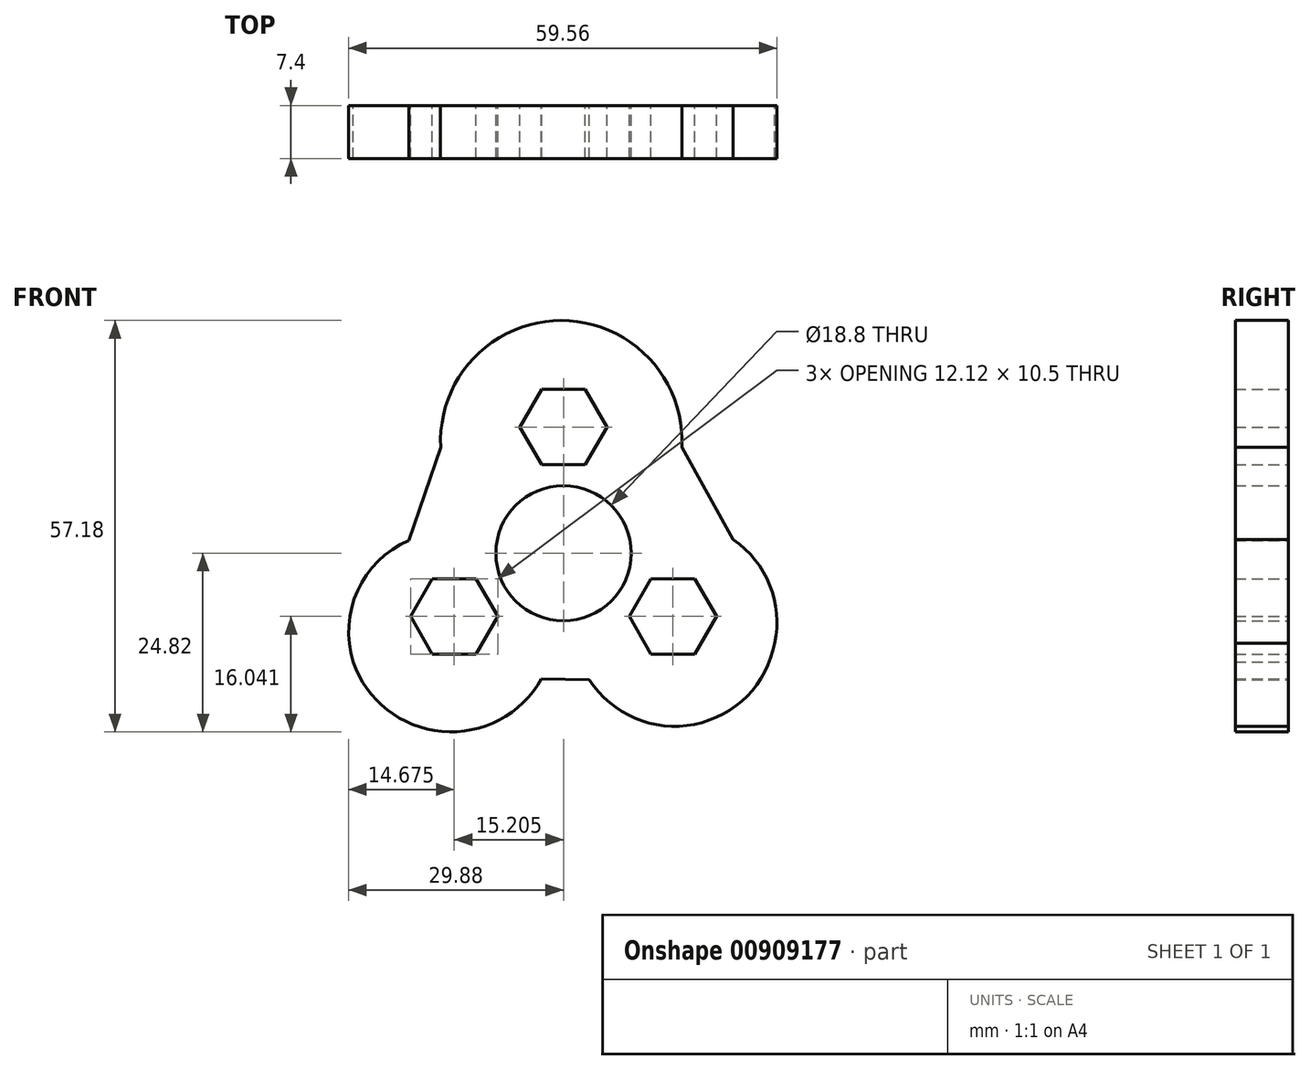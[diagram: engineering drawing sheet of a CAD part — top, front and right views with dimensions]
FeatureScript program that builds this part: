
annotation { "Feature Type Name" : "Feature", "Feature Type Description" : "" }
export const myFeature = defineFeature(function(context is Context, id is Id, definition is map)
    precondition{}
    {
        {
            var Q0;
            Q0=qCreatedBy(makeId("Front.planeOp"),FACE);
            var sketch = newSketch(context, id + "F0", { "sketchPlane" : qUnion([Q0])});
            skCircle(sketch, "E0", {"center": v(0, 0) * mm, "radius": 9.4 * mm});
            skLineSegment(sketch, "E1.0", {"start": v(3.03, 12.3) * mm, "end": v(-3.03, 12.3) * mm});
            skLineSegment(sketch, "E1.1", {"start": v(-3.03, 12.3) * mm, "end": v(-6.06, 17.56) * mm});
            skLineSegment(sketch, "E1.2", {"start": v(-6.06, 17.56) * mm, "end": v(-3.03, 22.8) * mm});
            skLineSegment(sketch, "E1.3", {"start": v(-3.03, 22.8) * mm, "end": v(3.03, 22.8) * mm});
            skLineSegment(sketch, "E1.4", {"start": v(3.03, 22.8) * mm, "end": v(6.06, 17.56) * mm});
            skLineSegment(sketch, "E1.5", {"start": v(6.06, 17.56) * mm, "end": v(3.03, 12.3) * mm});
            skPoint(sketch, "E1.0.midPoint", {"position": v(0, 12.3) * mm});
            skLineSegment(sketch, "E2.1.2", {"start": v(-18.24, -14.03) * mm, "end": v(-21.27, -8.78) * mm});
            skLineSegment(sketch, "E2.1.3", {"start": v(-21.27, -8.78) * mm, "end": v(-18.24, -3.53) * mm});
            skLineSegment(sketch, "E2.1.5", {"start": v(-18.24, -3.53) * mm, "end": v(-12.17, -3.53) * mm});
            skLineSegment(sketch, "E2.1.6", {"start": v(-12.17, -3.53) * mm, "end": v(-9.14, -8.78) * mm});
            skLineSegment(sketch, "E2.1.7", {"start": v(-9.14, -8.78) * mm, "end": v(-12.17, -14.03) * mm});
            skLineSegment(sketch, "E2.1.8", {"start": v(-12.17, -14.03) * mm, "end": v(-18.24, -14.03) * mm});
            skLineSegment(sketch, "E2.2.2", {"start": v(21.27, -8.78) * mm, "end": v(18.24, -14.03) * mm});
            skLineSegment(sketch, "E2.2.3", {"start": v(18.24, -14.03) * mm, "end": v(12.17, -14.03) * mm});
            skLineSegment(sketch, "E2.2.5", {"start": v(12.17, -14.03) * mm, "end": v(9.14, -8.78) * mm});
            skLineSegment(sketch, "E2.2.6", {"start": v(9.14, -8.78) * mm, "end": v(12.17, -3.53) * mm});
            skLineSegment(sketch, "E2.2.7", {"start": v(12.17, -3.53) * mm, "end": v(18.24, -3.53) * mm});
            skLineSegment(sketch, "E2.2.8", {"start": v(18.24, -3.53) * mm, "end": v(21.27, -8.78) * mm});
            skPoint(sketch, "E3.visualSharp", {"position": v(0, 48.24) * mm});
            skPoint(sketch, "E4.visualSharp", {"position": v(-41.78, -24.12) * mm});
            skPoint(sketch, "E5.visualSharp", {"position": v(41.78, -24.12) * mm});
            skArc(sketch, "E6", {"start": v(3.6, -17.6) * mm, "mid": v(18.21, -23.78) * mm, "end": v(29.37, -12.5) * mm});
            skArc(sketch, "E7", {"start": v(29.37, -12.5) * mm, "mid": v(28.68, -4.42) * mm, "end": v(23.61, 1.9) * mm});
            skArc(sketch, "E8", {"start": v(-29.24, -15.1) * mm, "mid": v(-16.92, -24.76) * mm, "end": v(-3.07, -17.46) * mm});
            skArc(sketch, "E9", {"start": v(-21.52, 1.77) * mm, "mid": v(-28.63, -5.19) * mm, "end": v(-29.24, -15.1) * mm});
            skLineSegment(sketch, "E10", {"start": v(-3.07, -17.46) * mm, "end": v(3.6, -17.6) * mm});
            skLineSegment(sketch, "E11", {"start": v(-17.07, 14.72) * mm, "end": v(-21.52, 1.77) * mm});
            skArc(sketch, "E12", {"start": v(16.46, 14.72) * mm, "mid": v(-0.3, 32.36) * mm, "end": v(-17.07, 14.72) * mm});
            skLineSegment(sketch, "E13", {"start": v(16.46, 14.72) * mm, "end": v(23.61, 1.9) * mm});
            skSolve(sketch);
        }
        {
            var Q0;
            Q0=makeQuery(id+"F0.imprint","IMPRINT",FACE,{"disambiguationData":[TD([[makeQuery(id+"F0.imprint","IMPRINT",EDGE,{"derivedFrom":sQuery(id+"F0.wireOp",EDGE,"E0")}),-1.0]])]});
            extrude(context, id + "F1", {"entities" : qUnion([Q0]), "depth" : 7.4 * mm, "offsetDistance" : 25 * mm});
        }
    });
